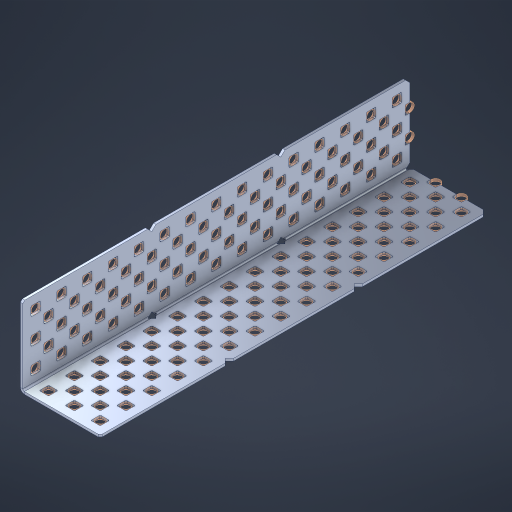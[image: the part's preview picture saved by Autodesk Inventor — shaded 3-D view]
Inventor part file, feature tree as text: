
AUTODESK INVENTOR PART (.ipt)
format: ipt  version: 2023 (Build 270158000, 158)  size: 1,744,896 bytes
history: native  units: in
note: dims shown in document units (in); Inventor stores cm internally (conversion verified against a paired STEP export)
features: other x156, extrude x148, sheet_metal_op x8, sketch x7, pattern_linear x3, mirror x1, chamfer x1
ambient origin geometry x8: Origin, YZ Plane, XZ Plane, XY Plane, X Axis, Y Axis, Z Axis, Center Point
bodies: Solid1 (feature_tree), Body (feature_tree)
feature tree (324):
  sheet_metal_op  "Flanges"
  sheet_metal_op  "Body Pattern"
  pattern_linear  "Center Double"  Spacing1=1.5in  [1 undecoded]
  pattern_linear  "Center Pattern"  Spacing1=0.1875in  [1 undecoded]
  other  "Arc Length"
  pattern_linear  "Notch Pattern"  Spacing1=0.0469in  [1 undecoded]
  other  "Diagonal Plane"
  mirror  "Everything Mirrored"
  chamfer  "End Chamfer"
  sketch  "Sketch1"  dims[d0=1.5in]
  other  "Plate1"
  sketch  "Sketch2"  dims[d1=7.5in]
  other  "Plate2"
  sheet_metal_op  "Bend1"
  sheet_metal_op  "Corner1"
  sketch  "Sketch8"  dims[d2=0.0469in]
  sketch  "Sketch9"  dims[d3=0.0469in]
  other  "Srf91"
  sheet_metal_op  "Body Pattern Sketch"
  other  "Srf92"
  sketch  "Sketch13"  dims[d4=0.0234in]
  sketch  "Sketch15"  dims[d5=0.0938in]
  sketch  "Sketch16"  dims[d6=0.0469in d7=1.5in d8=90.0deg d9=0.0312in d10=0.1875in d11=0.0469in d12=0.0469in d49=0.182in d50=0.02in d52=0.25in d53=0.0469in d54=0.0in d55=0.172in d56=1.0in d57=0.0in d85=0.1473in d86=0.1659in d89=0.0469in d90=0.0in d91=0.04in d92=0.0491in d95=2.5in d96=0.04in d97=0.25in d98=45.0deg d106=0.182in d107=0.02in d110=0.0469in d111=0.0in d112=0.172in d113=0.5in d114=0.0in d117=0.5in d126=0.0491in d127=0.1227in d128=0.08in d129=0.04in d130=2.5in d131=0.25in d132=5.9055in d134=0.5in d135=1.1811in d137=0.5in d140=0.5in d141=1.0in d142=0.3937in d144=0.5in d145=0.071in d146=0.7874in d148=0.5in]
  other  "Srf786"
  other  "Srf856"
  other  "Srf889"
  other  "Srf890"
  other  "Srf891"
  other  "Srf1275"
  other  "Srf1276"
  other  "Srf1278"
  other  "Srf1277"
  other  "Srf1285"
  other  "Srf1286"
  other  "Srf1287"
  other  "Srf1445"
  other  "Srf1446"
  other  "Srf1447"
  other  "Srf1448"
  other  "Srf1449"
  other  "Srf1537"
  other  "Srf1538"
  other  "Srf1539"
  other  "Srf1540"
  other  "Srf1541"
  other  "Srf1807"
  other  "Srf1808"
  other  "Srf1809"
  other  "Srf1810"
  other  "Srf1811"
  other  "Srf1812"
  other  "Srf1959"
  other  "Srf1960"
  other  "Srf1961"
  other  "Srf1962"
  other  "Srf1963"
  other  "Srf1964"
  other  "Srf2009"
  other  "Srf2010"
  other  "Srf2011"
  other  "Srf2012"
  other  "Srf2013"
  other  "Srf2014"
  other  "Srf2015"
  other  "Srf2016"
  other  "Srf2017"
  other  "Srf2018"
  other  "Srf2019"
  other  "Srf2020"
  other  "Srf2021"
  other  "Srf2022"
  other  "Srf2023"
  other  "Srf2043"
  other  "Srf2044"
  other  "Srf2045"
  other  "Srf2046"
  other  "Srf2047"
  other  "Srf2048"
  other  "Srf2049"
  other  "Srf2050"
  other  "Srf2051"
  other  "Srf2052"
  other  "Srf2053"
  other  "Srf2054"
  other  "Srf2055"
  other  "Srf2056"
  other  "Srf2076"
  other  "Srf2077"
  other  "Srf2078"
  other  "Srf2079"
  other  "Srf2080"
  other  "Srf2081"
  other  "Srf2082"
  other  "Srf2083"
  other  "Srf2084"
  other  "Srf2085"
  other  "Srf2086"
  other  "Srf2087"
  other  "Srf2088"
  other  "Srf2089"
  other  "Srf2090"
  other  "Srf2091"
  other  "Srf2092"
  other  "Srf2093"
  other  "Srf2094"
  other  "Srf2095"
  other  "Srf2096"
  other  "Srf2097"
  other  "Srf2098"
  other  "Srf2099"
  other  "Srf2100"
  other  "Srf2101"
  other  "Srf2102"
  other  "Srf2103"
  other  "Srf2104"
  other  "Srf2105"
  other  "Srf2106"
  other  "Srf2107"
  other  "Srf2108"
  other  "Srf2109"
  other  "Srf2110"
  other  "Srf2111"
  other  "Srf2112"
  other  "Srf2113"
  other  "Srf2114"
  other  "Srf2115"
  other  "Srf2116"
  other  "Srf2117"
  other  "Srf2118"
  other  "Srf2179"
  other  "Srf2180"
  other  "Srf2181"
  other  "Srf2182"
  other  "Srf2183"
  other  "Srf2184"
  other  "Srf2185"
  other  "Srf2186"
  other  "Srf2187"
  other  "Srf2188"
  other  "Srf2189"
  other  "Srf2190"
  other  "Srf2191"
  other  "Srf2192"
  other  "Srf2193"
  other  "Srf2194"
  other  "Srf2195"
  other  "Srf2196"
  other  "Srf2197"
  other  "Srf2198"
  other  "Srf2199"
  other  "Srf2200"
  other  "Srf2201"
  other  "Srf2202"
  other  "Srf2203"
  other  "Srf2204"
  other  "Srf2205"
  other  "Srf2206"
  other  "Srf2207"
  other  "Srf2208"
  other  "Srf2209"
  other  "Srf2210"
  other  "Srf2211"
  other  "Srf2212"
  other  "Srf2213"
  other  "Srf2214"
  other  "Srf2215"
  other  "Srf2216"
  other  "Srf2217"
  other  "Srf2218"
  other  "Srf2219"
  other  "Srf2220"
  sheet_metal_op  "Body Stamp"
  sheet_metal_op  "Body Circle"
  other  "Center Stamp"
  other  "Center Circle"
  sheet_metal_op  "Notch"
  extrude  "ExtrusionSrf92"  Depth=0.0469in
  extrude  "ExtrusionSrf856"  Depth=0.3937in
  extrude  "ExtrusionSrf889"  Depth=0.3937in
  extrude  "ExtrusionSrf890"  Depth=0.25in
  extrude  "ExtrusionSrf891"  Depth=0.0469in
  extrude  "ExtrusionSrf1275"  TaperAngle=0.0deg  [1 undecoded]
  extrude  "ExtrusionSrf1276"  Depth=0.3937in
  extrude  "ExtrusionSrf1277"  Depth=0.3937in TaperAngle=0.0deg
  extrude  "ExtrusionSrf1345"  Depth=0.3937in
  extrude  "ExtrusionSrf1346"  Depth=0.3937in
  extrude  "ExtrusionSrf1347"  Depth=0.0469in
  extrude  "ExtrusionSrf1348"  Depth=0.3937in TaperAngle=0.0deg
  extrude  "ExtrusionSrf1445"  Depth=0.3937in
  extrude  "ExtrusionSrf1446"  Depth=0.25in TaperAngle=45.0deg
  extrude  "ExtrusionSrf1447"  Depth=0.3937in
  extrude  "ExtrusionSrf1448"  Depth=0.3937in
  extrude  "ExtrusionSrf1449"  Depth=0.0469in
  extrude  "ExtrusionSrf1537"  TaperAngle=0.0deg  [1 undecoded]
  extrude  "ExtrusionSrf1538"  Depth=0.3937in
  extrude  "ExtrusionSrf1539"  Depth=0.3937in TaperAngle=0.0deg
  extrude  "ExtrusionSrf1540"  Depth=0.3937in
  extrude  "ExtrusionSrf1541"  Depth=0.3937in
  extrude  "ExtrusionSrf1807"  Depth=0.3937in
  extrude  "ExtrusionSrf1808"  Depth=0.3937in
  extrude  "ExtrusionSrf1809"  Depth=0.3937in
  extrude  "ExtrusionSrf1810"  Depth=0.3937in
  extrude  "ExtrusionSrf1811"  Depth=0.25in
  extrude  "ExtrusionSrf1812"  Depth=0.3937in
  extrude  "ExtrusionSrf1959"  Depth=0.3937in
  extrude  "ExtrusionSrf1960"  Depth=0.3937in
  extrude  "ExtrusionSrf1961"  Depth=0.3937in
  extrude  "ExtrusionSrf1962"  Depth=0.3937in
  extrude  "ExtrusionSrf1963"  Depth=0.3937in
  extrude  "ExtrusionSrf1964"  Depth=0.3937in
  extrude  "ExtrusionSrf2009"  [1 undecoded]
  extrude  "ExtrusionSrf2010"  [1 undecoded]
  extrude  "ExtrusionSrf2011"  [1 undecoded]
  extrude  "ExtrusionSrf2012"  [1 undecoded]
  extrude  "ExtrusionSrf2013"  [1 undecoded]
  extrude  "ExtrusionSrf2014"  [1 undecoded]
  extrude  "ExtrusionSrf2015"  [1 undecoded]
  extrude  "ExtrusionSrf2016"  [1 undecoded]
  extrude  "ExtrusionSrf2017"  [1 undecoded]
  extrude  "ExtrusionSrf2018"  [1 undecoded]
  extrude  "ExtrusionSrf2019"  [1 undecoded]
  extrude  "ExtrusionSrf2020"  [1 undecoded]
  extrude  "ExtrusionSrf2021"  [1 undecoded]
  extrude  "ExtrusionSrf2022"  [1 undecoded]
  extrude  "ExtrusionSrf2023"  [1 undecoded]
  extrude  "ExtrusionSrf2043"  [1 undecoded]
  extrude  "ExtrusionSrf2044"  [1 undecoded]
  extrude  "ExtrusionSrf2045"  [1 undecoded]
  extrude  "ExtrusionSrf2046"  [1 undecoded]
  extrude  "ExtrusionSrf2047"  [1 undecoded]
  extrude  "ExtrusionSrf2048"  [1 undecoded]
  extrude  "ExtrusionSrf2049"  [1 undecoded]
  extrude  "ExtrusionSrf2050"  [1 undecoded]
  extrude  "ExtrusionSrf2051"  [1 undecoded]
  extrude  "ExtrusionSrf2052"  [1 undecoded]
  extrude  "ExtrusionSrf2053"  [1 undecoded]
  extrude  "ExtrusionSrf2054"  [1 undecoded]
  extrude  "ExtrusionSrf2055"  [1 undecoded]
  extrude  "ExtrusionSrf2056"  [1 undecoded]
  extrude  "ExtrusionSrf2076"  [1 undecoded]
  extrude  "ExtrusionSrf2077"  [1 undecoded]
  extrude  "ExtrusionSrf2078"  [1 undecoded]
  extrude  "ExtrusionSrf2079"  [1 undecoded]
  extrude  "ExtrusionSrf2080"  [1 undecoded]
  extrude  "ExtrusionSrf2081"  [1 undecoded]
  extrude  "ExtrusionSrf2082"  [1 undecoded]
  extrude  "ExtrusionSrf2083"  [1 undecoded]
  extrude  "ExtrusionSrf2084"  [1 undecoded]
  extrude  "ExtrusionSrf2085"  [1 undecoded]
  extrude  "ExtrusionSrf2086"  [1 undecoded]
  extrude  "ExtrusionSrf2087"  [1 undecoded]
  extrude  "ExtrusionSrf2088"  [1 undecoded]
  extrude  "ExtrusionSrf2089"  [1 undecoded]
  extrude  "ExtrusionSrf2090"  [1 undecoded]
  extrude  "ExtrusionSrf2091"  [1 undecoded]
  extrude  "ExtrusionSrf2092"  [1 undecoded]
  extrude  "ExtrusionSrf2093"  [1 undecoded]
  extrude  "ExtrusionSrf2094"  [1 undecoded]
  extrude  "ExtrusionSrf2095"  [1 undecoded]
  extrude  "ExtrusionSrf2096"  [1 undecoded]
  extrude  "ExtrusionSrf2097"  [1 undecoded]
  extrude  "ExtrusionSrf2098"  [1 undecoded]
  extrude  "ExtrusionSrf2099"  [1 undecoded]
  extrude  "ExtrusionSrf2100"  [1 undecoded]
  extrude  "ExtrusionSrf2101"  [1 undecoded]
  extrude  "ExtrusionSrf2102"  [1 undecoded]
  extrude  "ExtrusionSrf2103"  [1 undecoded]
  extrude  "ExtrusionSrf2104"  [1 undecoded]
  extrude  "ExtrusionSrf2105"  [1 undecoded]
  extrude  "ExtrusionSrf2106"  [1 undecoded]
  extrude  "ExtrusionSrf2107"  [1 undecoded]
  extrude  "ExtrusionSrf2108"  [1 undecoded]
  extrude  "ExtrusionSrf2109"  [1 undecoded]
  extrude  "ExtrusionSrf2110"  [1 undecoded]
  extrude  "ExtrusionSrf2111"  [1 undecoded]
  extrude  "ExtrusionSrf2112"  [1 undecoded]
  extrude  "ExtrusionSrf2113"  [1 undecoded]
  extrude  "ExtrusionSrf2114"  [1 undecoded]
  extrude  "ExtrusionSrf2115"  [1 undecoded]
  extrude  "ExtrusionSrf2116"  [1 undecoded]
  extrude  "ExtrusionSrf2117"  [1 undecoded]
  extrude  "ExtrusionSrf2118"  [1 undecoded]
  extrude  "ExtrusionSrf2179"  [1 undecoded]
  extrude  "ExtrusionSrf2180"  [1 undecoded]
  extrude  "ExtrusionSrf2181"  [1 undecoded]
  extrude  "ExtrusionSrf2182"  [1 undecoded]
  extrude  "ExtrusionSrf2183"  [1 undecoded]
  extrude  "ExtrusionSrf2184"  [1 undecoded]
  extrude  "ExtrusionSrf2185"  [1 undecoded]
  extrude  "ExtrusionSrf2186"  [1 undecoded]
  extrude  "ExtrusionSrf2187"  [1 undecoded]
  extrude  "ExtrusionSrf2188"  [1 undecoded]
  extrude  "ExtrusionSrf2189"  [1 undecoded]
  extrude  "ExtrusionSrf2190"  [1 undecoded]
  extrude  "ExtrusionSrf2191"  [1 undecoded]
  extrude  "ExtrusionSrf2192"  [1 undecoded]
  extrude  "ExtrusionSrf2193"  [1 undecoded]
  extrude  "ExtrusionSrf2194"  [1 undecoded]
  extrude  "ExtrusionSrf2195"  [1 undecoded]
  extrude  "ExtrusionSrf2196"  [1 undecoded]
  extrude  "ExtrusionSrf2197"  [1 undecoded]
  extrude  "ExtrusionSrf2198"  [1 undecoded]
  extrude  "ExtrusionSrf2199"  [1 undecoded]
  extrude  "ExtrusionSrf2200"  [1 undecoded]
  extrude  "ExtrusionSrf2201"  [1 undecoded]
  extrude  "ExtrusionSrf2202"  [1 undecoded]
  extrude  "ExtrusionSrf2203"  [1 undecoded]
  extrude  "ExtrusionSrf2204"  [1 undecoded]
  extrude  "ExtrusionSrf2205"  [1 undecoded]
  extrude  "ExtrusionSrf2206"  [1 undecoded]
  extrude  "ExtrusionSrf2207"  [1 undecoded]
  extrude  "ExtrusionSrf2208"  [1 undecoded]
  extrude  "ExtrusionSrf2209"  [1 undecoded]
  extrude  "ExtrusionSrf2210"  [1 undecoded]
  extrude  "ExtrusionSrf2211"  [1 undecoded]
  extrude  "ExtrusionSrf2212"  [1 undecoded]
  extrude  "ExtrusionSrf2213"  [1 undecoded]
  extrude  "ExtrusionSrf2214"  [1 undecoded]
  extrude  "ExtrusionSrf2215"  [1 undecoded]
  extrude  "ExtrusionSrf2216"  [1 undecoded]
  extrude  "ExtrusionSrf2217"  [1 undecoded]
  extrude  "ExtrusionSrf2218"  [1 undecoded]
  extrude  "ExtrusionSrf2219"  [1 undecoded]
  extrude  "ExtrusionSrf2220"  [1 undecoded]
note: 119 required parameter values undecoded (feature->parameter linkage not recoverable at this tier; creation-order binding heuristic only, values carry confidence <= 0.55)
